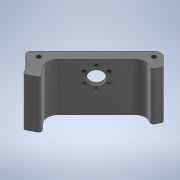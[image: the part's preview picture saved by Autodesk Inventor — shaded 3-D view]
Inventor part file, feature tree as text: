
AUTODESK INVENTOR PART (.ipt)
format: ipt  version: 2020 (Build 240168000, 168)  size: 393,728 bytes
history: native  units: mm
features: extrude x4, sketch x3, other x1, chamfer x1, fillet x1
ambient origin geometry x8: Origin, YZ Plane, XZ Plane, XY Plane, X Axis, Y Axis, Z Axis, Center Point
bodies: Body1 (feature_tree)
feature tree (10):
  other  "Твердое тело1"
  sketch  "Эскиз1"
  extrude  "Выдавливание10"  Depth=3.0mm
  sketch  "Эскиз6"
  extrude  "Выдавливание13"  Depth=6.0mm
  extrude  "Выдавливание14"  Depth=35.0mm TaperAngle=0.0deg
  chamfer  "Фаска3"  Distance=59.0mm
  extrude  "Выдавливание15"  Depth=21.2mm
  fillet  "Сопряжение1"  Radius=15.0mm
  sketch  "Эскиз7"
